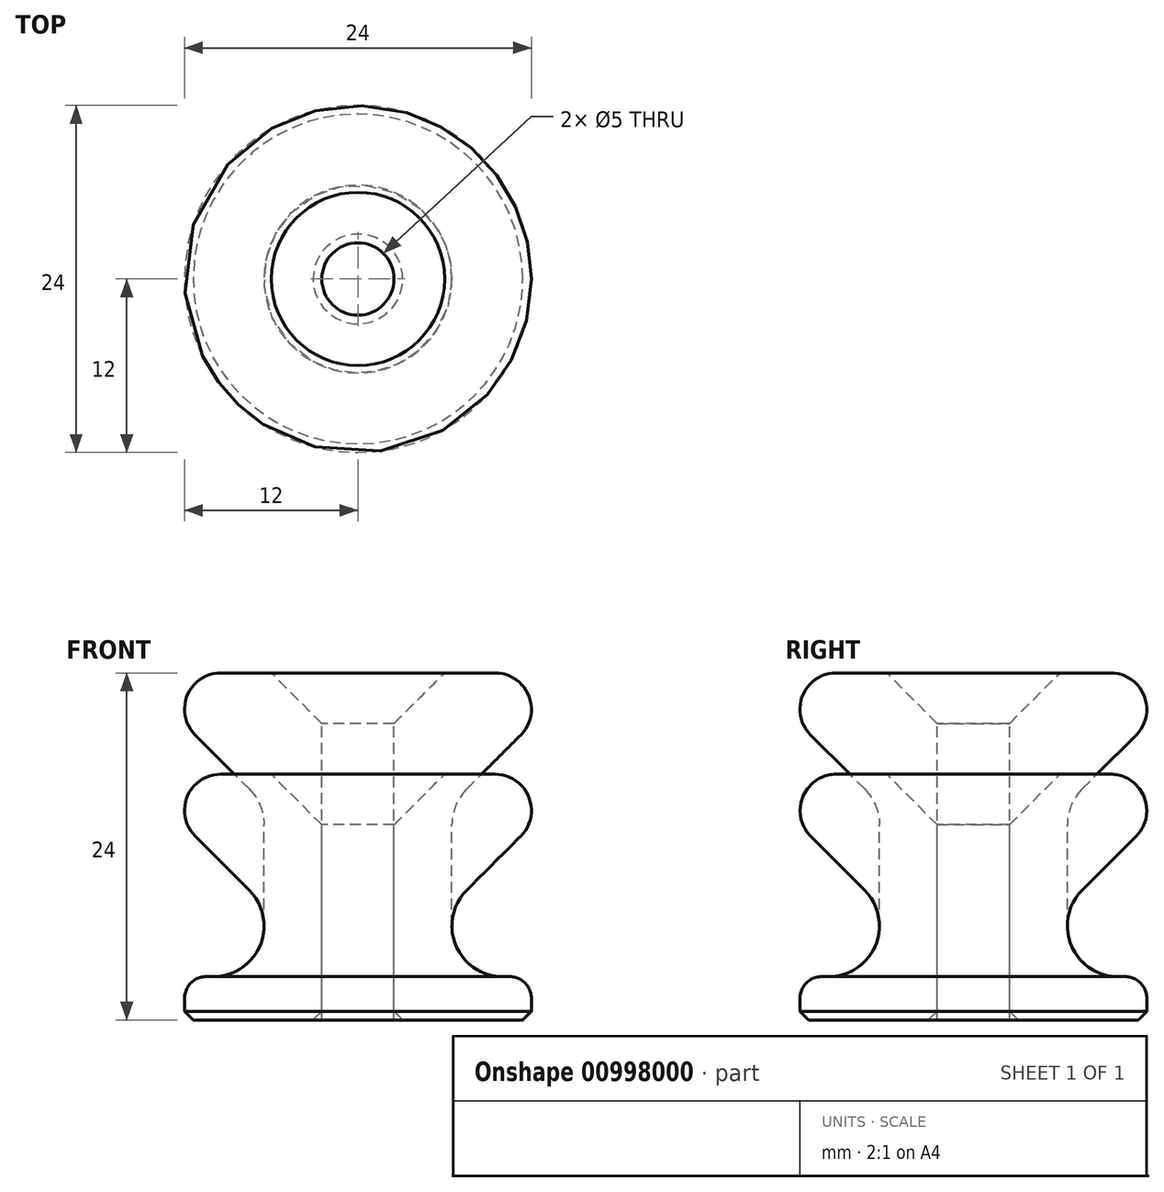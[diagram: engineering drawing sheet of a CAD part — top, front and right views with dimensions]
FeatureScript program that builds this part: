
annotation { "Feature Type Name" : "Feature", "Feature Type Description" : "" }
export const myFeature = defineFeature(function(context is Context, id is Id, definition is map)
    precondition{}
    {
        {
            var Q0;
            Q0=qCreatedBy(makeId("Front.planeOp"),FACE);
            var sketch = newSketch(context, id + "F0", { "sketchPlane" : qUnion([Q0])});
            skLineSegment(sketch, "E0", {"start": v(0, 13.1) * mm, "end": v(0, -18.84) * mm, "construction": true});
            skLineSegment(sketch, "E1", {"start": v(-2.5, 0) * mm, "end": v(-2.5, 17) * mm});
            skCircle(sketch, "E2", {"center": v(-10, 6.5) * mm, "radius": 3.5 * mm});
            skLineSegment(sketch, "E3", {"start": v(-10, 3) * mm, "end": v(-10.5, 3) * mm});
            skLineSegment(sketch, "E4", {"start": v(-12, 1.5) * mm, "end": v(-12, 0) * mm});
            skLineSegment(sketch, "E5", {"start": v(-12, 0) * mm, "end": v(-2.5, 0) * mm});
            skLineSegment(sketch, "E6", {"start": v(-7.53, 8.97) * mm, "end": v(-11.26, 12.71) * mm});
            skCircle(sketch, "E7", {"center": v(-9.49, 14.49) * mm, "radius": 2.51 * mm});
            skLineSegment(sketch, "E8", {"start": v(-9.49, 17) * mm, "end": v(-2.5, 17) * mm});
            skLineSegment(sketch, "E9", {"start": v(-12, 14.49) * mm, "end": v(-12, 23.7) * mm, "construction": true});
            skLineSegment(sketch, "E10", {"start": v(-6, 17) * mm, "end": v(-2.5, 13.5) * mm});
            skLineSegment(sketch, "E11", {"start": v(-12, 0.6) * mm, "end": v(-11.4, 0) * mm});
            skLineSegment(sketch, "E12", {"start": v(-2.5, 0.6) * mm, "end": v(-3.1, 0) * mm});
            skPoint(sketch, "E13.visualSharp", {"position": v(-12, 3) * mm});
            skArc(sketch, "E13.filletArc", {"start": v(-10.5, 3) * mm, "mid": v(-11.56, 2.56) * mm, "end": v(-12, 1.5) * mm});
            skSolve(sketch);
        }
        {
            var Q0;
            {var subQ0=sQuery(id+"F0.wireOp",EDGE,"E3");Q0=makeQuery(id+"F0.imprint","IMPRINT",FACE,{"disambiguationData":[TD([[makeQuery(id+"F0.imprint","IMPRINT",EDGE,{"derivedFrom":subQ0}),1.0]])]});}
            var Q1;
            {var subQ0=sQuery(id+"F0.wireOp",EDGE,"E7");var subQ1=makeQuery(id+"F0.imprint","INTERSECT",VERTEX,{"derivedFrom":[sQuery(id+"F0.wireOp",EDGE,"E6"),subQ0]});Q1=makeQuery(id+"F0.imprint","IMPRINT",FACE,{"disambiguationData":[TD([[makeQuery(id+"F0.imprint","IMPRINT",EDGE,{"disambiguationData":[TD([[subQ1,1.0]])],"derivedFrom":subQ0}),1.0]])]});}
            var Q2;
            Q2=sQuery(id+"F0.wireOp",EDGE,"E0");
            revolve(context, id + "F1", {"surfaceOperationType" : NewSurfaceOperationType.NEW, "entities" : qUnion([Q0, Q1]), "axis" : qUnion([Q2]), "revolveType" : RevolveType.FULL});
        }
        {
            var Q0;
            Q0=qCreatedBy(makeId("Front.planeOp"),FACE);
            var sketch = newSketch(context, id + "F2", { "sketchPlane" : qUnion([Q0])});
            skLineSegment(sketch, "E14.0", {"start": v(-11.4, 0) * mm, "end": v(11.4, 0) * mm});
            skLineSegment(sketch, "E15.0", {"start": v(-12, 0.6) * mm, "end": v(12, 0.6) * mm});
            skLineSegment(sketch, "E16.0", {"start": v(-12, 1.5) * mm, "end": v(12, 1.5) * mm});
            skLineSegment(sketch, "E17", {"start": v(-10.5, 3) * mm, "end": v(10.5, 3) * mm});
            skArc(sketch, "E18", {"start": v(-10.5, 3) * mm, "mid": v(-11.56, 2.56) * mm, "end": v(-12, 1.5) * mm});
            skLineSegment(sketch, "E19", {"start": v(-12, 0.6) * mm, "end": v(-12, 1.5) * mm});
            skLineSegment(sketch, "E20", {"start": v(-11.4, 0) * mm, "end": v(-12, 0.6) * mm});
            skLineSegment(sketch, "E21", {"start": v(2.5, 13.5) * mm, "end": v(2.5, 0.6) * mm});
            skLineSegment(sketch, "E22", {"start": v(-2.5, 0.6) * mm, "end": v(-2.5, 13.5) * mm});
            skLineSegment(sketch, "E23", {"start": v(6, 17) * mm, "end": v(2.5, 13.5) * mm});
            skArc(sketch, "E24", {"start": v(-10, 3) * mm, "mid": v(-6.77, 5.16) * mm, "end": v(-7.53, 8.97) * mm});
            skCircle(sketch, "E25", {"center": v(-10, 6.5) * mm, "radius": 3.5 * mm});
            skCircle(sketch, "E26", {"center": v(-10, 13.5) * mm, "radius": 3.5 * mm});
            skLineSegment(sketch, "E27", {"start": v(-6.5, 6.5) * mm, "end": v(-6.5, 13.5) * mm});
            skLineSegment(sketch, "E28", {"start": v(-7.53, 15.97) * mm, "end": v(-11.26, 19.71) * mm});
            skArc(sketch, "E29", {"start": v(-9.49, 24) * mm, "mid": v(-11.8, 22.45) * mm, "end": v(-11.26, 19.71) * mm});
            skLineSegment(sketch, "E30", {"start": v(-9.49, 24) * mm, "end": v(-2.5, 24) * mm});
            skLineSegment(sketch, "E31", {"start": v(-2.5, 24) * mm, "end": v(-2.5, 13.5) * mm});
            skLineSegment(sketch, "E32", {"start": v(-12, 21.49) * mm, "end": v(-12, 16.84) * mm, "construction": true});
            skArc(sketch, "E33", {"start": v(-9.49, 17) * mm, "mid": v(-11.8, 15.45) * mm, "end": v(-11.26, 12.71) * mm, "construction": true});
            skLineSegment(sketch, "E34", {"start": v(-6, 24) * mm, "end": v(-2.5, 20.5) * mm});
            skLineSegment(sketch, "E35", {"start": v(0, 24.1) * mm, "end": v(0, -4.2) * mm, "construction": true});
            skLineSegment(sketch, "E36", {"start": v(-11.4, 0) * mm, "end": v(-2.5, 0) * mm});
            skLineSegment(sketch, "E37", {"start": v(-2.5, 0) * mm, "end": v(-2.5, 0.6) * mm});
            skSolve(sketch);
        }
        {
            var Q0;
            {var subQ0=sQuery(id+"F2.wireOp",EDGE,"E27");Q0=makeQuery(id+"F2.imprint","IMPRINT",FACE,{"disambiguationData":[TD([[makeQuery(id+"F2.imprint","IMPRINT",EDGE,{"derivedFrom":subQ0}),-1.0]])]});}
            var Q1;
            {var subQ4=sQuery(id+"F2.wireOp",EDGE,"E18");Q1=makeQuery(id+"F2.imprint","IMPRINT",FACE,{"disambiguationData":[TD([[makeQuery(id+"F2.imprint","IMPRINT",EDGE,{"derivedFrom":subQ4}),1.0]])]});}
            var Q2;
            {var subQ0=sQuery(id+"F2.wireOp",EDGE,"E19");Q2=makeQuery(id+"F2.imprint","IMPRINT",FACE,{"disambiguationData":[TD([[makeQuery(id+"F2.imprint","IMPRINT",EDGE,{"derivedFrom":subQ0}),-1.0]])]});}
            var Q3;
            {var subQ0=sQuery(id+"F2.wireOp",EDGE,"E20");Q3=makeQuery(id+"F2.imprint","IMPRINT",FACE,{"disambiguationData":[TD([[makeQuery(id+"F2.imprint","IMPRINT",EDGE,{"derivedFrom":subQ0}),-1.0]])]});}
            var Q4;
            Q4=sQuery(id+"F2.wireOp",EDGE,"E35");
            revolve(context, id + "F3", {"surfaceOperationType" : NewSurfaceOperationType.NEW, "entities" : qUnion([Q0, Q1, Q2, Q3]), "axis" : qUnion([Q4]), "revolveType" : RevolveType.FULL});
        }
    });
